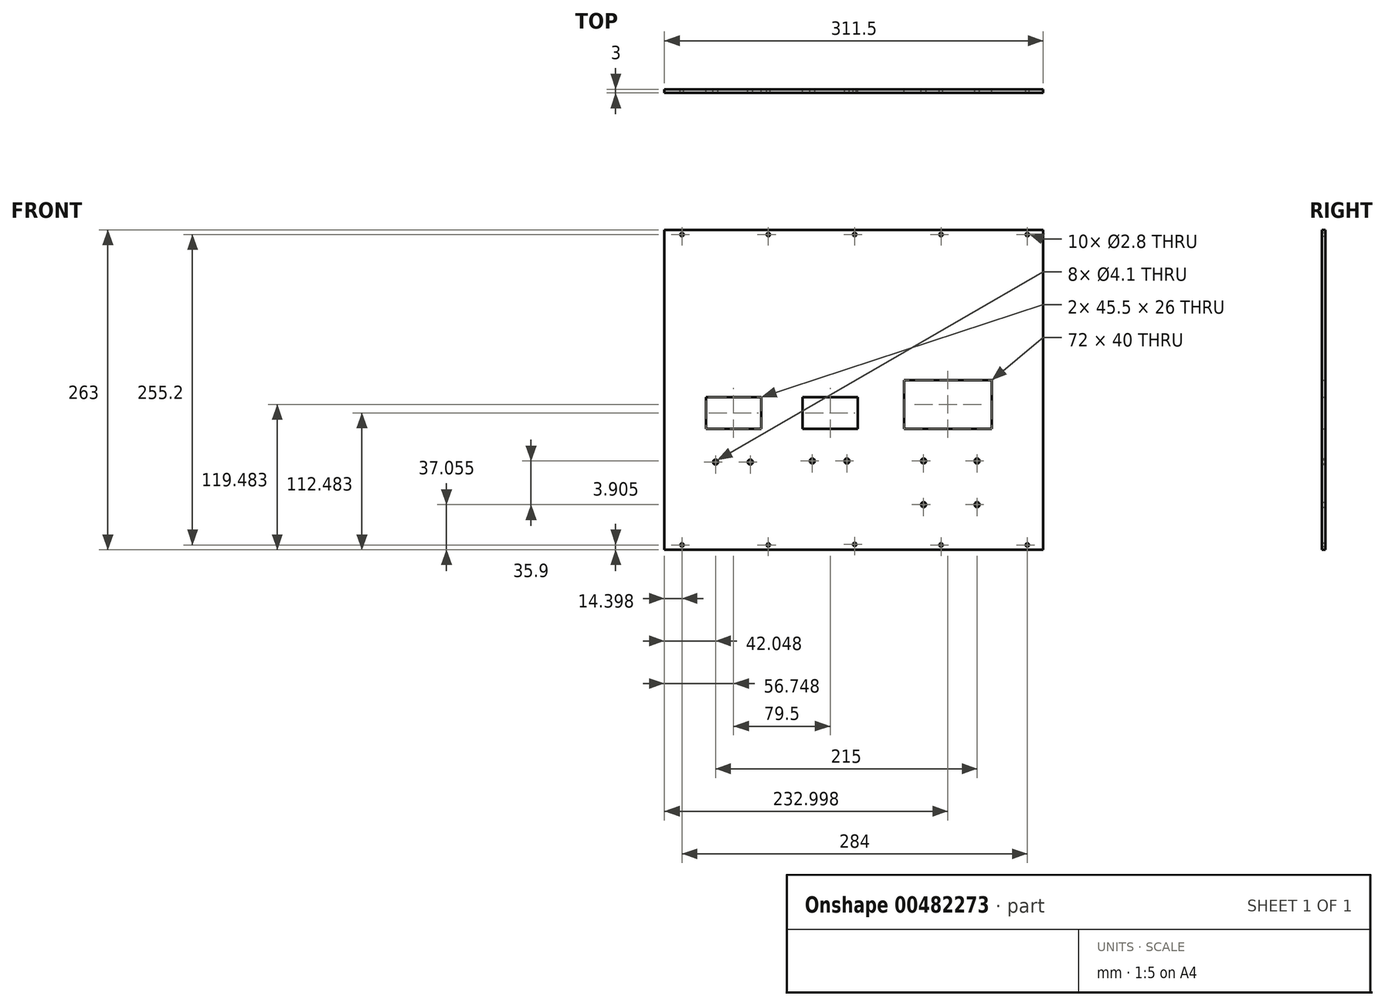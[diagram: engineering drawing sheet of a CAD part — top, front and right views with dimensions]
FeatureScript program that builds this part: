
annotation { "Feature Type Name" : "Feature", "Feature Type Description" : "" }
export const myFeature = defineFeature(function(context is Context, id is Id, definition is map)
    precondition{}
    {
        {
            var Q0;
            Q0=qCreatedBy(makeId("Front.planeOp"),FACE);
            var sketch = newSketch(context, id + "F0", { "sketchPlane" : qUnion([Q0])});
            skLineSegment(sketch, "E0.bottom", {"start": v(-208.05, 149.63) * mm, "end": v(103.45, 149.63) * mm});
            skLineSegment(sketch, "E0.top", {"start": v(-208.05, -113.37) * mm, "end": v(103.45, -113.37) * mm});
            skLineSegment(sketch, "E0.left", {"start": v(-208.05, 149.63) * mm, "end": v(-208.05, -113.37) * mm});
            skLineSegment(sketch, "E0.right", {"start": v(103.45, 149.63) * mm, "end": v(103.45, -113.37) * mm});
            skCircle(sketch, "E1", {"center": v(-193.65, -109.47) * mm, "radius": 1.4 * mm});
            skCircle(sketch, "E2", {"center": v(-51.65, -108.97) * mm, "radius": 1.4 * mm});
            skCircle(sketch, "E3", {"center": v(90.35, -109.47) * mm, "radius": 1.4 * mm});
            skCircle(sketch, "E4", {"center": v(-193.65, 145.73) * mm, "radius": 1.4 * mm});
            skCircle(sketch, "E5", {"center": v(-51.65, 145.73) * mm, "radius": 1.4 * mm});
            skCircle(sketch, "E6", {"center": v(90.35, 145.73) * mm, "radius": 1.4 * mm});
            skLineSegment(sketch, "E7.bottom", {"start": v(-11.05, 26.11) * mm, "end": v(60.95, 26.11) * mm});
            skLineSegment(sketch, "E7.top", {"start": v(-11.05, -13.89) * mm, "end": v(60.95, -13.89) * mm});
            skLineSegment(sketch, "E7.left", {"start": v(-11.05, 26.11) * mm, "end": v(-11.05, -13.89) * mm});
            skLineSegment(sketch, "E7.right", {"start": v(60.95, 26.11) * mm, "end": v(60.95, -13.89) * mm});
            skLineSegment(sketch, "E8.bottom", {"start": v(-94.55, 12.11) * mm, "end": v(-49.05, 12.11) * mm});
            skLineSegment(sketch, "E8.top", {"start": v(-94.55, -13.89) * mm, "end": v(-49.05, -13.89) * mm});
            skLineSegment(sketch, "E8.left", {"start": v(-94.55, 12.11) * mm, "end": v(-94.55, -13.89) * mm});
            skLineSegment(sketch, "E8.right", {"start": v(-49.05, 12.11) * mm, "end": v(-49.05, -13.89) * mm});
            skLineSegment(sketch, "E9.bottom", {"start": v(-174.05, 12.11) * mm, "end": v(-128.55, 12.11) * mm});
            skLineSegment(sketch, "E9.top", {"start": v(-174.05, -13.89) * mm, "end": v(-128.55, -13.89) * mm});
            skLineSegment(sketch, "E9.left", {"start": v(-174.05, 12.11) * mm, "end": v(-174.05, -13.89) * mm});
            skLineSegment(sketch, "E9.right", {"start": v(-128.55, 12.11) * mm, "end": v(-128.55, -13.89) * mm});
            skCircle(sketch, "E10", {"center": v(-166, -41.32) * mm, "radius": 2.05 * mm});
            skCircle(sketch, "E11", {"center": v(-137.5, -41.32) * mm, "radius": 2.05 * mm});
            skCircle(sketch, "E12", {"center": v(-86.5, -40.42) * mm, "radius": 2.05 * mm});
            skCircle(sketch, "E13", {"center": v(-58, -40.42) * mm, "radius": 2.05 * mm});
            skCircle(sketch, "E14", {"center": v(5, -40.42) * mm, "radius": 2.05 * mm});
            skCircle(sketch, "E15", {"center": v(49, -40.42) * mm, "radius": 2.05 * mm});
            skCircle(sketch, "E16", {"center": v(49, -76.32) * mm, "radius": 2.05 * mm});
            skCircle(sketch, "E17", {"center": v(5, -76.32) * mm, "radius": 2.05 * mm});
            skCircle(sketch, "E18", {"center": v(-122.65, -109.47) * mm, "radius": 1.4 * mm});
            skCircle(sketch, "E19", {"center": v(19.35, -109.47) * mm, "radius": 1.4 * mm});
            skCircle(sketch, "E20", {"center": v(-122.65, 145.73) * mm, "radius": 1.4 * mm});
            skCircle(sketch, "E21", {"center": v(19.35, 145.73) * mm, "radius": 1.4 * mm});
            skSolve(sketch);
        }
        {
            var Q0;
            Q0=makeQuery(id+"F0.imprint","IMPRINT",FACE,{"disambiguationData":[TD([[makeQuery(id+"F0.imprint","IMPRINT",EDGE,{"derivedFrom":sQuery(id+"F0.wireOp",EDGE,"E0.bottom")}),-1.0]])]});
            extrude(context, id + "F1", {"entities" : qUnion([Q0]), "depth" : 3 * mm, "offsetDistance" : 25 * mm});
        }
    });
